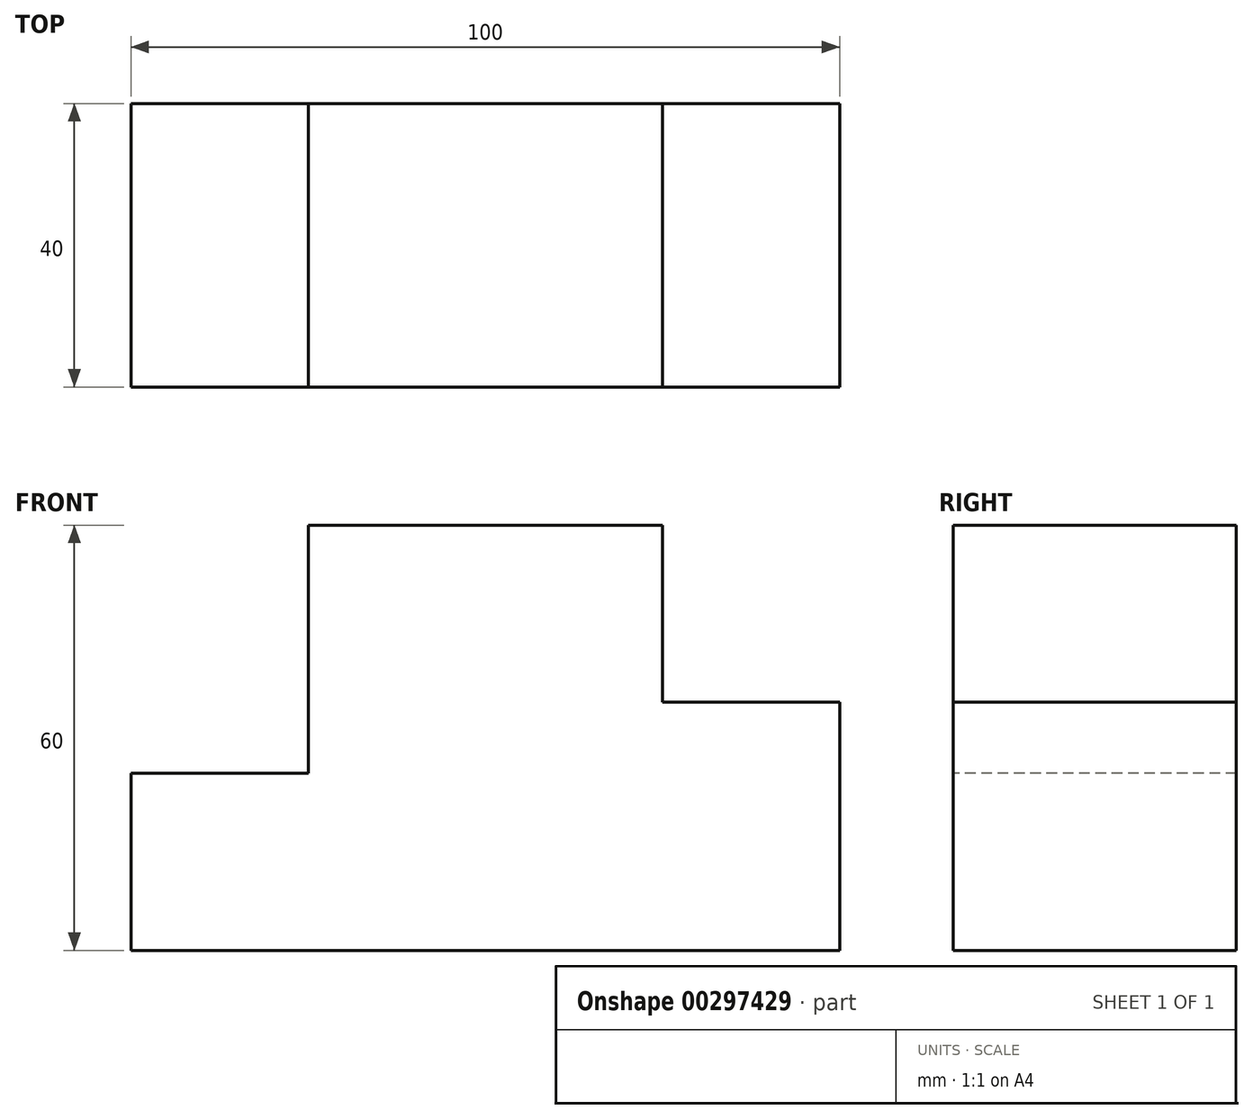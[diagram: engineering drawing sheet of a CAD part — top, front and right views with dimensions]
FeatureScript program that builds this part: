
annotation { "Feature Type Name" : "Feature", "Feature Type Description" : "" }
export const myFeature = defineFeature(function(context is Context, id is Id, definition is map)
    precondition{}
    {
        {
            var Q0;
            Q0=qCreatedBy(makeId("Front.planeOp"),FACE);
            var sketch = newSketch(context, id + "F0", { "sketchPlane" : qUnion([Q0])});
            skLineSegment(sketch, "E0.bottom", {"start": v(50, -30) * mm, "end": v(-50, -30) * mm});
            skLineSegment(sketch, "E0.top", {"start": v(50, 30) * mm, "end": v(-50, 30) * mm});
            skLineSegment(sketch, "E0.left", {"start": v(50, -30) * mm, "end": v(50, 30) * mm});
            skLineSegment(sketch, "E0.right", {"start": v(-50, -30) * mm, "end": v(-50, 30) * mm});
            skPoint(sketch, "E0.middle", {"position": v(0, 0) * mm});
            skSolve(sketch);
        }
        {
            var Q0;
            Q0=makeQuery(id+"F0.imprint","IMPRINT",FACE,{"disambiguationData":[TD([[makeQuery(id+"F0.imprint","IMPRINT",EDGE,{"derivedFrom":sQuery(id+"F0.wireOp",EDGE,"E0.bottom")}),-1.0]])]});
            extrude(context, id + "F1", {"entities" : qUnion([Q0]), "depth" : 40 * mm});
        }
        {
            var Q0;
            Q0=makeQuery(id+"F1.opExtrude","CAP_FACE",FACE,{"disambiguationData":[OSD([sQuery(id+"F0.wireOp",EDGE,"E0.bottom"),sQuery(id+"F0.wireOp",EDGE,"E0.top"),sQuery(id+"F0.wireOp",EDGE,"E0.left"),sQuery(id+"F0.wireOp",EDGE,"E0.right")])],"isStart":false});
            var sketch = newSketch(context, id + "F2", { "sketchPlane" : qUnion([Q0])});
            skLineSegment(sketch, "E1.bottom", {"start": v(50, 30) * mm, "end": v(25, 30) * mm});
            skLineSegment(sketch, "E1.top", {"start": v(50, 5) * mm, "end": v(25, 5) * mm});
            skLineSegment(sketch, "E1.left", {"start": v(50, 30) * mm, "end": v(50, 5) * mm});
            skLineSegment(sketch, "E1.right", {"start": v(25, 30) * mm, "end": v(25, 5) * mm});
            skLineSegment(sketch, "E2.bottom", {"start": v(-50, 30) * mm, "end": v(-25, 30) * mm});
            skLineSegment(sketch, "E2.top", {"start": v(-50, -5) * mm, "end": v(-25, -5) * mm});
            skLineSegment(sketch, "E2.left", {"start": v(-50, 30) * mm, "end": v(-50, -5) * mm});
            skLineSegment(sketch, "E2.right", {"start": v(-25, 30) * mm, "end": v(-25, -5) * mm});
            skSolve(sketch);
        }
        {
            var Q0;
            Q0=makeQuery(id+"F2.imprint","IMPRINT",FACE,{"disambiguationData":[TD([[makeQuery(id+"F2.imprint","IMPRINT",EDGE,{"derivedFrom":sQuery(id+"F2.wireOp",EDGE,"E2.bottom")}),1.0]])]});
            var Q1;
            Q1=makeQuery(id+"F2.imprint","IMPRINT",FACE,{"disambiguationData":[TD([[makeQuery(id+"F2.imprint","IMPRINT",EDGE,{"derivedFrom":sQuery(id+"F2.wireOp",EDGE,"E1.bottom")}),1.0]])]});
            extrude(context, id + "F3", {"entities" : qUnion([Q0, Q1]), "operationType" : NewBodyOperationType.REMOVE, "endBound" : BoundingType.THROUGH_ALL, "oppositeDirection" : true, "depth" : 25 * mm});
        }
    });
